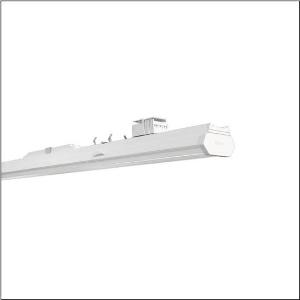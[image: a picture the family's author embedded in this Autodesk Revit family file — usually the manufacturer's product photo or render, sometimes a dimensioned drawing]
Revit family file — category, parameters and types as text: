
# Revit family: licross_r__21_protected_mo_52tp11dn4axg_b280
name_source: partatom
category: Lighting Fixtures
units: mm (PartAtom-declared; Revit-internal decimal feet)

## family parameters
Cut with Voids When Loaded = No
Host = Face
Light Source = No
Part Type = Normal
Room Calculation Point = No
Round Connector Dimension = Use Diameter
Shared = No

## types (1)
- --- (1 x LED, 10000 lm, 57.8 W, 4000K)
    Apparent Load = 58 VA
    CIE Flux Codes = 83 94 98 100 100
    Color Rendering = 80
    Color Temperature = 4000K
    Default Elevation = 1800 mm
    Description = Licross® 21 Protected MO, luminaire insert, of sheet steel, galvanised, coil coated, white, length: 1.500mm, width: 90mm, height: 103mm, LED rated luminous flux: 10.000lm, light colour: 840, SDCM (Standard Deviation of Colour Matching)MacAdam ≤ 3 SDCM (initial), control gear: DALI 2, with plug, 5-pole, with phase selection, mains connection: 220..240V, AC, 50/60Hz, rated input power: 58W, internal wiring halogen-free, primary light control with lens, of plastic, primary optical cover: cover, of PMMA, light emission: direct distribution, primary light characteristic: symmetric, protection rating (complete): IP64, insulation class (complete): insulation class I (protective earthing), certification: CE, ENEC, VDE, UKCA, protection symbol: D if used in an environment with conductive dust loads with corresponding accessories, impact resistance: IK06, permissible ambient temperature for indoor applications: -25..+40°C, corresponds to IFS (International Featured Standards) requirements for safety and quality in the food industry, reducing of maximum allowable ambient temperature of 5°C with ceiling mounting, LABS conformity tested according to VDMA 24364:2018-05, packaging unit: 1 piece
    Height = 92 mm
    Lamp = 1 x LED
    Lamp Light Flux = 10000 lm
    Lamp Power = 57.8 W
    Lamp count = 1
    Length = 1500 mm
    Luminous efficacy = 173 lm/W
    Manufacturer = Siteco
    ModVariant = No
    Model = 52TP11DN4AXG
    Mounting Place = Ceiling
    Mounting Type = Pendant
    Number of Poles = 1
    OnlyDefault = Yes
    Power Factor = 1
    Product Name = Licross® 21 Protected MO
    Product group = luminaire insert | ceiling pendant
    ProductGroupID = 901
    Protection Class = Protection class I
    Protection Degree = IP 64
    RLX_Detail_Level = 1
    RLX_Emergency_Light_Flux = 0 lm
    RLX_Emergency_Type = 0
    RLX_Emergency_Type_DB = No
    RlxData = <blob elided: 24149 chars, md5=43f421e2>
    Socket = socket
    Standby Power = 0 W
    System Light Flux = 10000 lm
    System Power = 58 W
    Type Comments = factory setting: luminous flux: 100 % | dim-lin: 254 | 390 mA
    Type Image = l_1256148.jpg
    URL = http://relux.com
    VarID = @adj_132081
    Voltage = 0 V
    Weight = 0.00 kg
    Width = 88 mm

## geometry (parser evidence)
native form markers: Blend x4, Sweep x11
no freeform markers — native parametric forms only
